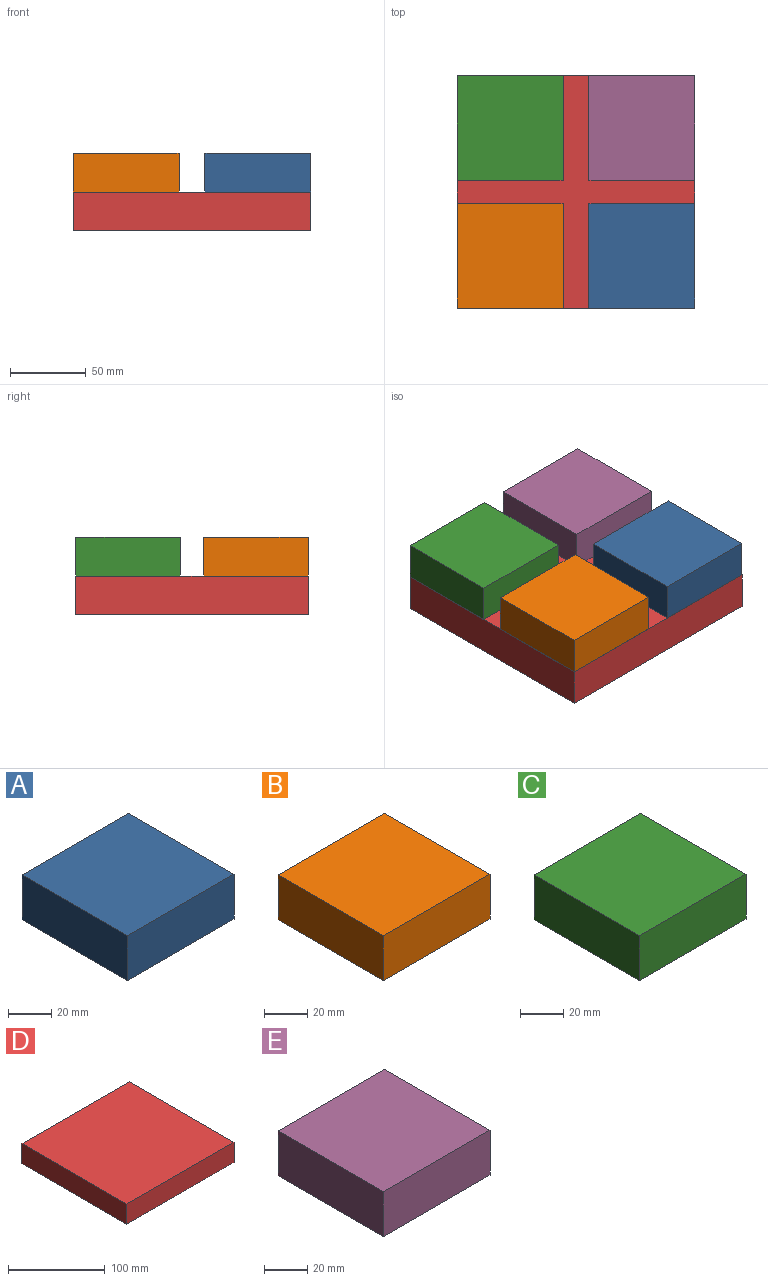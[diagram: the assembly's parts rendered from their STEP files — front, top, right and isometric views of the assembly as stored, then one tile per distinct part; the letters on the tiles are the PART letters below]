
ASSEMBLY  parts=5 mates=4
PART A: 6 faces, bbox 69.6x68.8x25.4 mm
  f0: plane 68.78x25.4mm, normal (-1,0,0), area 1747.1mm2, adj f1,f3,f4,f5
  f1: plane 69.65x25.4mm, normal (0,-1,0), area 1769mm2, adj f0,f2,f4,f5
  f2: plane 68.78x25.4mm, normal (1,0,0), area 1747.1mm2, adj f1,f3,f4,f5
  f3: plane 69.65x25.4mm, normal (0,1,0), area 1769mm2, adj f0,f2,f4,f5
  f4: plane 69.65x68.78mm, normal (0,0,1), area 4790.5mm2, adj f0,f1,f2,f3
  f5: plane 69.65x68.78mm, normal (0,0,-1), area 4790.5mm2, adj f0,f1,f2,f3
PART B: 6 faces, bbox 69.6x68.8x25.4 mm
  f0: plane 68.78x25.4mm, normal (-1,0,0), area 1747.1mm2, adj f1,f3,f4,f5
  f1: plane 69.65x25.4mm, normal (0,-1,0), area 1769mm2, adj f0,f2,f4,f5
  f2: plane 68.78x25.4mm, normal (1,0,0), area 1747.1mm2, adj f1,f3,f4,f5
  f3: plane 69.65x25.4mm, normal (0,1,0), area 1769mm2, adj f0,f2,f4,f5
  f4: plane 69.65x68.78mm, normal (0,0,1), area 4790.5mm2, adj f0,f1,f2,f3
  f5: plane 69.65x68.78mm, normal (0,0,-1), area 4790.5mm2, adj f0,f1,f2,f3
PART C: 6 faces, bbox 69.6x68.8x25.4 mm
  f0: plane 69.65x25.4mm, normal (0,1,0), area 1769.1mm2, adj f1,f3,f4,f5
  f1: plane 68.79x25.4mm, normal (-1,0,0), area 1747.2mm2, adj f0,f2,f4,f5
  f2: plane 69.65x25.4mm, normal (0,-1,0), area 1769.1mm2, adj f1,f3,f4,f5
  f3: plane 68.79x25.4mm, normal (1,0,0), area 1747.2mm2, adj f0,f2,f4,f5
  f4: plane 69.65x68.79mm, normal (0,0,1), area 4790.8mm2, adj f0,f1,f2,f3
  f5: plane 69.65x68.79mm, normal (0,0,-1), area 4790.8mm2, adj f0,f1,f2,f3
PART D: 6 faces, bbox 156.4x153x25.4 mm
  f0: plane 156.42x25.4mm, normal (0,-1,0), area 3973mm2, adj f1,f3,f4,f5
  f1: plane 153.04x25.4mm, normal (1,0,0), area 3887.2mm2, adj f0,f2,f4,f5
  f2: plane 156.42x25.4mm, normal (0,1,0), area 3973mm2, adj f1,f3,f4,f5
  f3: plane 153.04x25.4mm, normal (-1,0,0), area 3887.2mm2, adj f0,f2,f4,f5
  f4: plane 156.42x153.04mm, normal (0,0,1), area 23937.8mm2, adj f0,f1,f2,f3
  f5: plane 156.42x153.04mm, normal (0,0,-1), area 23937.8mm2, adj f0,f1,f2,f3
PART E: 6 faces, bbox 69.6x68.8x25.4 mm
  f0: plane 69.65x25.4mm, normal (0,1,0), area 1769mm2, adj f1,f3,f4,f5
  f1: plane 68.78x25.4mm, normal (-1,0,0), area 1747.1mm2, adj f0,f2,f4,f5
  f2: plane 69.65x25.4mm, normal (0,-1,0), area 1769mm2, adj f1,f3,f4,f5
  f3: plane 68.78x25.4mm, normal (1,0,0), area 1747.1mm2, adj f0,f2,f4,f5
  f4: plane 69.65x68.78mm, normal (0,0,1), area 4790.5mm2, adj f0,f1,f2,f3
  f5: plane 69.65x68.78mm, normal (0,0,-1), area 4790.5mm2, adj f0,f1,f2,f3
PLACE A t=(-11.62,4.03,-8.91)mm
PLACE B t=(-12.22,4.03,-8.91)mm
PLACE C t=(-12.22,4.24,-8.91)mm
PLACE D t=(-11.65,4.02,-59.71)mm
PLACE E t=(-11.62,4.24,-8.91)mm
MATE fastened D.f4 <-> C.f5  axis (0,0,1) through (-88.63,80.94,-8.91)mm
MATE fastened A.f5 <-> D.f4  axis (0,0,1) through (67.78,-72.1,-8.91)mm
MATE fastened E.f5 <-> D.f4  axis (0,0,1) through (67.78,80.94,-8.91)mm
MATE fastened B.f5 <-> D.f4  axis (0,0,1) through (-88.63,-72.1,-8.91)mm
